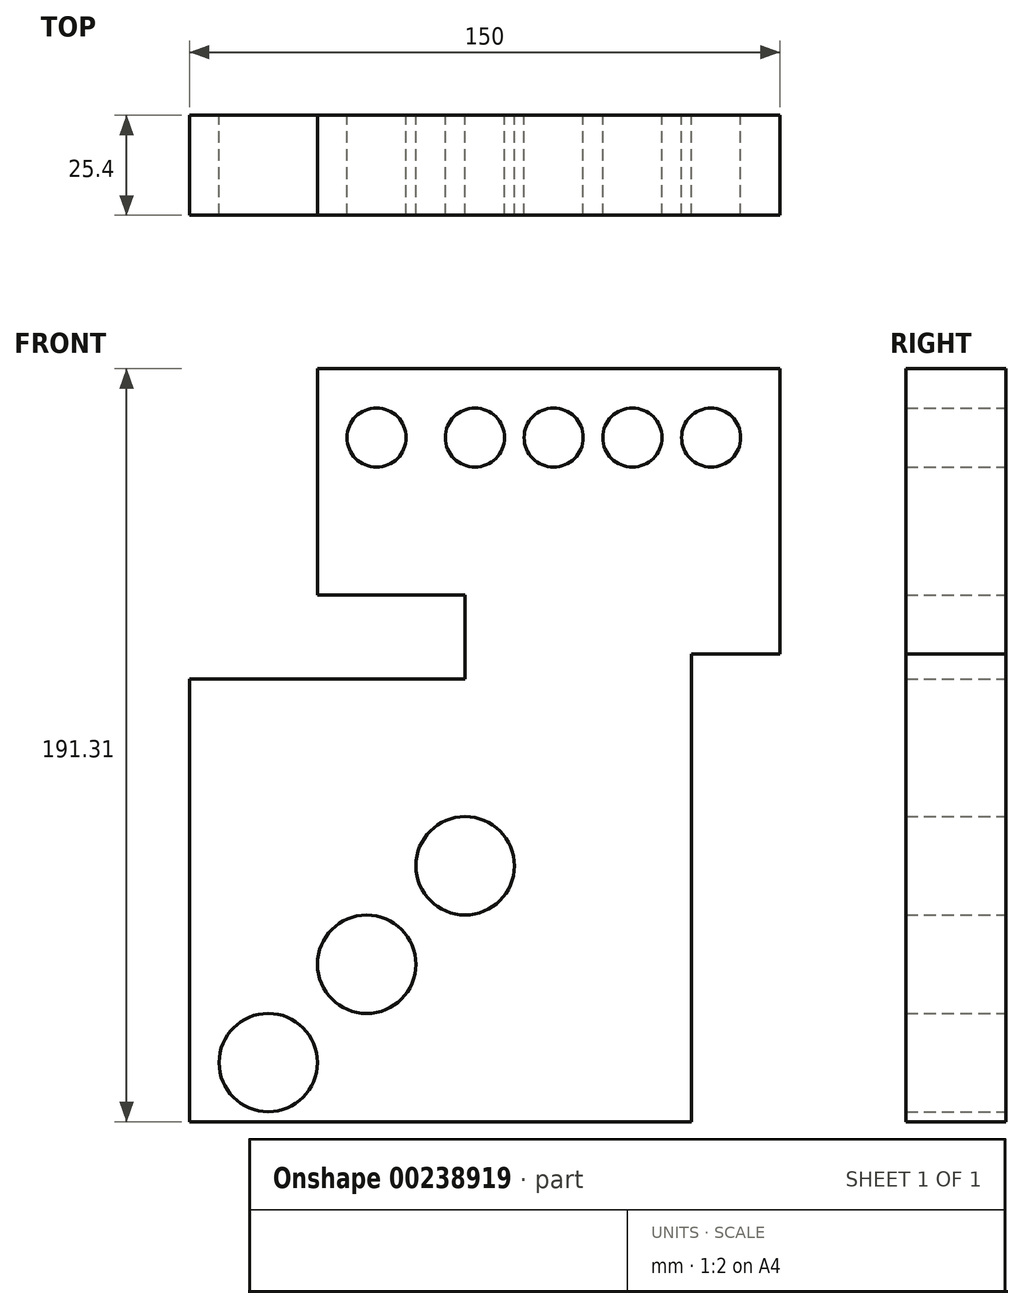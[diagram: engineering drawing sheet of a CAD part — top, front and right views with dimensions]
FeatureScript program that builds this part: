
annotation { "Feature Type Name" : "Feature", "Feature Type Description" : "" }
export const myFeature = defineFeature(function(context is Context, id is Id, definition is map)
    precondition{}
    {
        {
            var Q0;
            Q0=qCreatedBy(makeId("Front.planeOp"),FACE);
            var sketch = newSketch(context, id + "F0", { "sketchPlane" : qUnion([Q0])});
            skLineSegment(sketch, "E0.bottom", {"start": v(-82.17, 9.23) * mm, "end": v(45.33, 9.23) * mm});
            skLineSegment(sketch, "E0.top", {"start": v(-82.17, -103.27) * mm, "end": v(45.33, -103.27) * mm});
            skLineSegment(sketch, "E0.left", {"start": v(-82.17, 9.23) * mm, "end": v(-82.17, -103.27) * mm});
            skLineSegment(sketch, "E0.right", {"start": v(45.33, 9.23) * mm, "end": v(45.33, -103.27) * mm});
            skLineSegment(sketch, "E1", {"start": v(-82.17, 9.23) * mm, "end": v(-12.17, 9.23) * mm});
            skLineSegment(sketch, "E2", {"start": v(-12.17, 9.23) * mm, "end": v(-12.17, 30.54) * mm});
            skLineSegment(sketch, "E3", {"start": v(-12.17, 30.54) * mm, "end": v(-49.67, 30.54) * mm});
            skLineSegment(sketch, "E4", {"start": v(-49.67, 30.54) * mm, "end": v(-49.67, 88.04) * mm});
            skLineSegment(sketch, "E5", {"start": v(-49.67, 88.04) * mm, "end": v(67.83, 88.04) * mm});
            skLineSegment(sketch, "E6", {"start": v(67.83, 88.04) * mm, "end": v(67.83, 15.54) * mm});
            skLineSegment(sketch, "E7", {"start": v(45.33, 9.23) * mm, "end": v(45.33, 15.54) * mm});
            skLineSegment(sketch, "E8", {"start": v(67.83, 15.54) * mm, "end": v(45.33, 15.54) * mm});
            skLineSegment(sketch, "E9", {"start": v(67.83, 88.04) * mm, "end": v(67.83, 70.54) * mm});
            skCircle(sketch, "E10", {"center": v(50.33, 70.54) * mm, "radius": 7.5 * mm});
            skCircle(sketch, "E11", {"center": v(30.33, 70.54) * mm, "radius": 7.5 * mm});
            skCircle(sketch, "E12", {"center": v(10.33, 70.54) * mm, "radius": 7.5 * mm});
            skCircle(sketch, "E13", {"center": v(-9.67, 70.54) * mm, "radius": 7.5 * mm});
            skCircle(sketch, "E14", {"center": v(-34.67, 70.54) * mm, "radius": 7.5 * mm});
            skLineSegment(sketch, "E15", {"start": v(-82.17, -103.27) * mm, "end": v(-82.17, -88.27) * mm});
            skLineSegment(sketch, "E16", {"start": v(-82.17, -88.27) * mm, "end": v(-82.17, -63.27) * mm});
            skLineSegment(sketch, "E17", {"start": v(-82.17, -63.27) * mm, "end": v(-82.17, -38.27) * mm});
            skLineSegment(sketch, "E18", {"start": v(-82.17, -103.27) * mm, "end": v(-12.17, -103.27) * mm});
            skLineSegment(sketch, "E19", {"start": v(-12.17, -103.27) * mm, "end": v(-37.17, -103.27) * mm});
            skLineSegment(sketch, "E20", {"start": v(-37.17, -103.27) * mm, "end": v(-62.17, -103.27) * mm});
            skCircle(sketch, "E21", {"center": v(-12.17, -38.27) * mm, "radius": 12.5 * mm});
            skCircle(sketch, "E22", {"center": v(-37.17, -63.27) * mm, "radius": 12.5 * mm});
            skCircle(sketch, "E23", {"center": v(-62.17, -88.27) * mm, "radius": 12.5 * mm});
            skSolve(sketch);
        }
        {
            var Q0;
            Q0=makeQuery(id+"F0.imprint","IMPRINT",FACE,{"disambiguationData":[TD([[makeQuery(id+"F0.imprint","IMPRINT",EDGE,{"derivedFrom":sQuery(id+"F0.wireOp",EDGE,"E0.bottom")}),1.0]])]});
            var Q1;
            Q1=makeQuery(id+"F0.imprint","IMPRINT",FACE,{"disambiguationData":[TD([[makeQuery(id+"F0.imprint","IMPRINT",EDGE,{"derivedFrom":sQuery(id+"F0.wireOp",EDGE,"E0.bottom")}),-1.0]])]});
            extrude(context, id + "F1", {"entities" : qUnion([Q0, Q1]), "depth" : 25.4 * mm});
        }
    });
